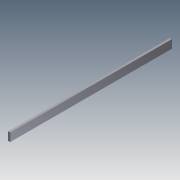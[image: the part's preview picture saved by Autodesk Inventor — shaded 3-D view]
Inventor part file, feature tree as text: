
AUTODESK INVENTOR PART (.ipt)
format: ipt  version: 2011 (Build 150239000, 239)  size: 67,072 bytes
history: native  units: in
note: dims shown in document units (in); Inventor stores cm internally (conversion verified against a paired STEP export)
features: extrude x1, sketch x1
ambient origin geometry x8: Origin, YZ Plane, XZ Plane, XY Plane, X Axis, Y Axis, Z Axis, Center Point
bodies: Solid1 (feature_tree)
feature tree (2):
  extrude  "Extrusion1"  Depth=1.0in
  sketch  "Sketch1"  dims[d0=0.25in d1=1.0in d2=19.5in d3=0.0in]
